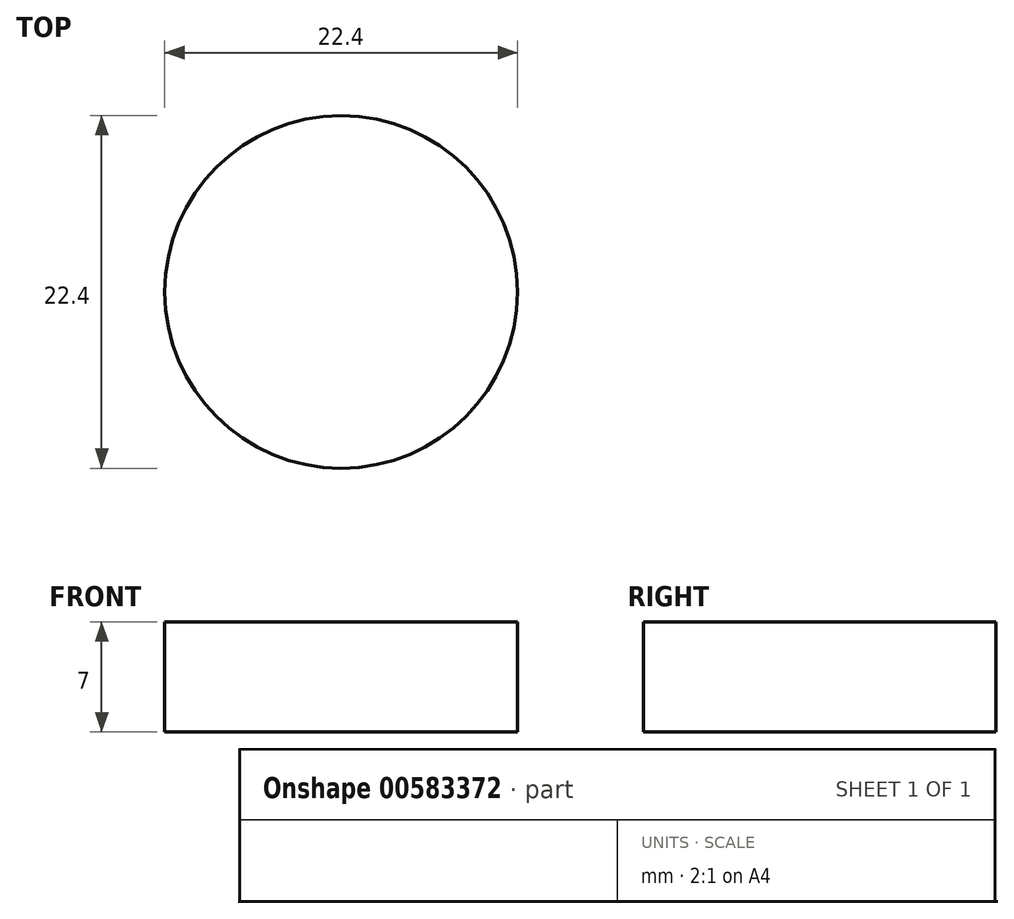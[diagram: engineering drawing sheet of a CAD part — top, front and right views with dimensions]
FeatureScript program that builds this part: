
annotation { "Feature Type Name" : "Feature", "Feature Type Description" : "" }
export const myFeature = defineFeature(function(context is Context, id is Id, definition is map)
    precondition{}
    {
        {
            var Q0;
            Q0=qCreatedBy(makeId("Top.planeOp"),FACE);
            var sketch = newSketch(context, id + "F0", { "sketchPlane" : qUnion([Q0])});
            skCircle(sketch, "E0", {"center": v(0, 0) * mm, "radius": 11.2 * mm});
            skCircle(sketch, "E1", {"center": v(0, 0) * mm, "radius": 13.2 * mm});
            skCircle(sketch, "E2", {"center": v(0, 26.45) * mm, "radius": 11.2 * mm});
            skCircle(sketch, "E3", {"center": v(0, 26.45) * mm, "radius": 13.2 * mm});
            skCircle(sketch, "E4.1.0", {"center": v(-23.1, -13.55) * mm, "radius": 13.2 * mm});
            skCircle(sketch, "E4.2.0", {"center": v(23.1, -13.56) * mm, "radius": 13.2 * mm});
            skPoint(sketch, "E4.center", {"position": v(0, -0.22) * mm});
            skArc(sketch, "E5", {"start": v(10.7, 18.73) * mm, "mid": v(11.62, 6.98) * mm, "end": v(20.66, -0.58) * mm});
            skArc(sketch, "E6.1.0", {"start": v(-21.58, -0.1) * mm, "mid": v(-11.85, 6.57) * mm, "end": v(-9.83, 18.19) * mm});
            skArc(sketch, "E6.2.0", {"start": v(10.87, -18.64) * mm, "mid": v(0.23, -13.55) * mm, "end": v(-10.84, -17.6) * mm});
            skSolve(sketch);
        }
        {
            var Q0;
            Q0=makeQuery(id+"F0.imprint","IMPRINT",FACE,{"disambiguationData":[TD([[makeQuery(id+"F0.imprint","IMPRINT",EDGE,{"derivedFrom":sQuery(id+"F0.wireOp",EDGE,"E0")}),1.0]])]});
            extrude(context, id + "F1", {"entities" : qUnion([Q0]), "depth" : 7 * mm, "offsetDistance" : 25 * mm});
        }
    });
